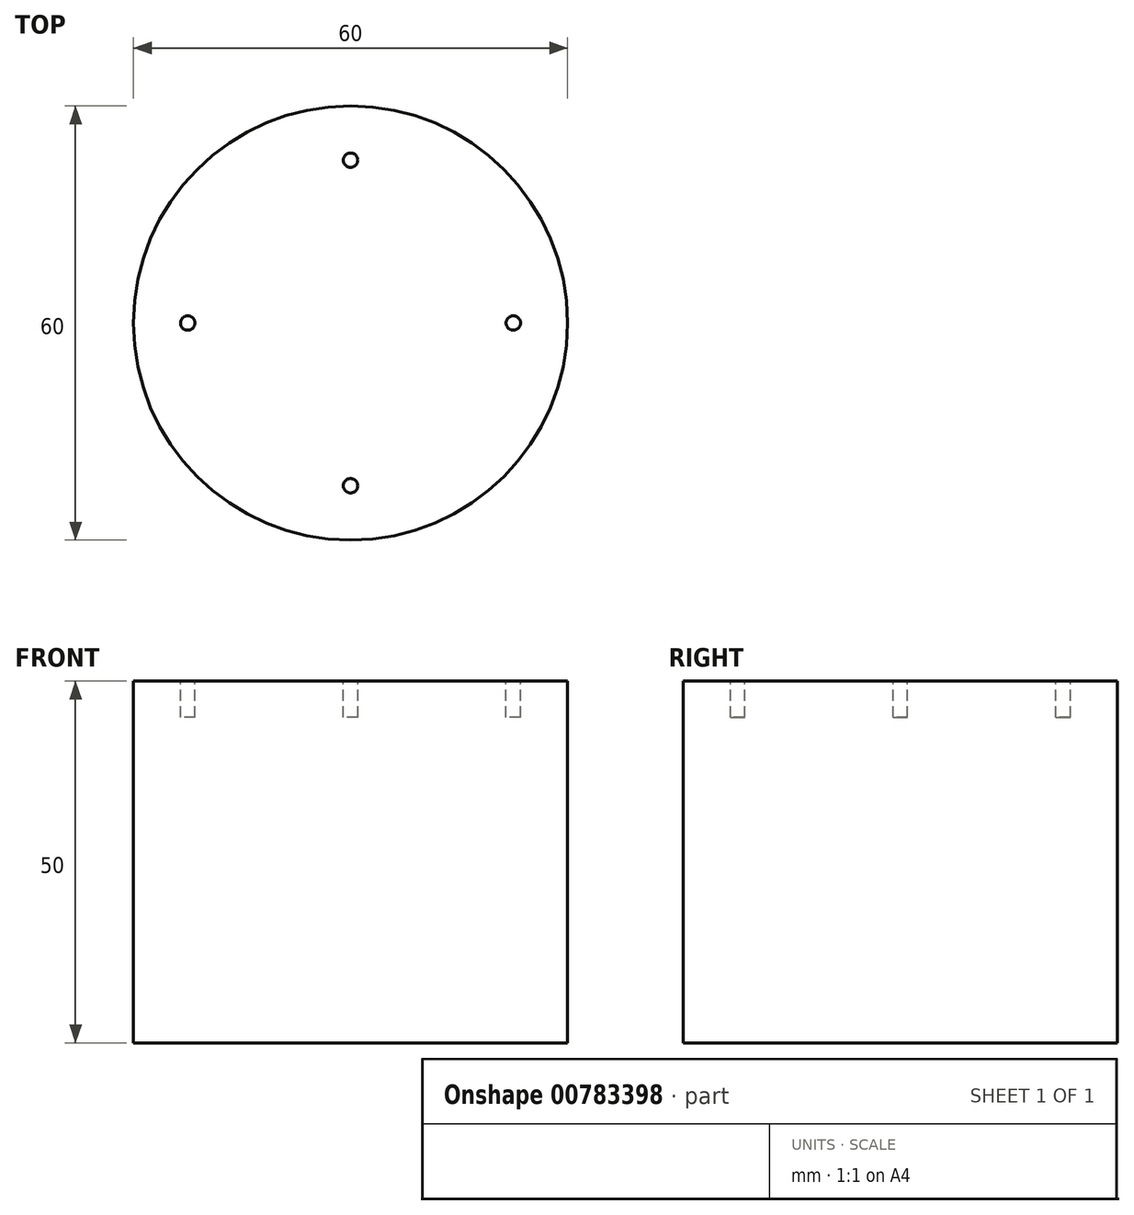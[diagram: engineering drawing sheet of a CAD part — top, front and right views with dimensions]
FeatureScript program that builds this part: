
annotation { "Feature Type Name" : "Feature", "Feature Type Description" : "" }
export const myFeature = defineFeature(function(context is Context, id is Id, definition is map)
    precondition{}
    {
        {
            var Q0;
            Q0=qCreatedBy(makeId("Top.planeOp"),FACE);
            var sketch = newSketch(context, id + "F0", { "sketchPlane" : qUnion([Q0])});
            skCircle(sketch, "E0", {"center": v(0, 0) * mm, "radius": 30 * mm});
            skSolve(sketch);
        }
        {
            var Q0;
            Q0=makeQuery(id+"F0.imprint","IMPRINT",FACE,{"disambiguationData":[TD([[makeQuery(id+"F0.imprint","IMPRINT",EDGE,{"derivedFrom":sQuery(id+"F0.wireOp",EDGE,"E0")}),1.0]])]});
            extrude(context, id + "F1", {"entities" : qUnion([Q0]), "depth" : 50 * mm, "offsetDistance" : 25 * mm});
        }
        {
            var Q0;
            Q0=makeQuery(id+"F1.opExtrude","CAP_FACE",FACE,{"disambiguationData":[OSD([sQuery(id+"F0.wireOp",EDGE,"E0")])],"isStart":false});
            var sketch = newSketch(context, id + "F2", { "sketchPlane" : qUnion([Q0])});
            skCircle(sketch, "E1", {"center": v(22.5, 0) * mm, "radius": 1 * mm});
            skCircle(sketch, "E2", {"center": v(0, 22.5) * mm, "radius": 1 * mm});
            skCircle(sketch, "E3", {"center": v(-22.5, 0) * mm, "radius": 1 * mm});
            skCircle(sketch, "E4", {"center": v(0, -22.5) * mm, "radius": 1 * mm});
            skSolve(sketch);
        }
        {
            var Q0;
            Q0=makeQuery(id+"F2.imprint","IMPRINT",FACE,{"disambiguationData":[TD([[makeQuery(id+"F2.imprint","IMPRINT",EDGE,{"derivedFrom":sQuery(id+"F2.wireOp",EDGE,"E3")}),1.0]])]});
            var Q1;
            Q1=makeQuery(id+"F2.imprint","IMPRINT",FACE,{"disambiguationData":[TD([[makeQuery(id+"F2.imprint","IMPRINT",EDGE,{"derivedFrom":sQuery(id+"F2.wireOp",EDGE,"E2")}),1.0]])]});
            var Q2;
            Q2=makeQuery(id+"F2.imprint","IMPRINT",FACE,{"disambiguationData":[TD([[makeQuery(id+"F2.imprint","IMPRINT",EDGE,{"derivedFrom":sQuery(id+"F2.wireOp",EDGE,"E1")}),1.0]])]});
            var Q3;
            Q3=makeQuery(id+"F2.imprint","IMPRINT",FACE,{"disambiguationData":[TD([[makeQuery(id+"F2.imprint","IMPRINT",EDGE,{"derivedFrom":sQuery(id+"F2.wireOp",EDGE,"E4")}),1.0]])]});
            extrude(context, id + "F3", {"entities" : qUnion([Q0, Q1, Q2, Q3]), "operationType" : NewBodyOperationType.REMOVE, "oppositeDirection" : true, "depth" : 5 * mm, "offsetDistance" : 25 * mm});
        }
    });
